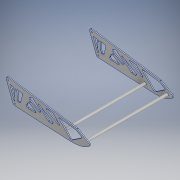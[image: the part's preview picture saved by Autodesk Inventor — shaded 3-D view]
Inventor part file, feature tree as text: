
AUTODESK INVENTOR PART (.ipt)
format: ipt  version: 2018.2 (Build 222227000, 227)  size: 1,288,192 bytes
history: native  units: mm
features: other x5, extrude x2, sketch x2, mirror x1
ambient origin geometry x8: Origin, YZ Plane, XZ Plane, XY Plane, X Axis, Y Axis, Z Axis, Center Point
bodies: Body1 (feature_tree)
feature tree (10):
  other  "bracket1.ipt"
  other  "作業平面1"
  mirror  "ミラー1"
  extrude  "押し出し1"  Depth=10.0mm
  extrude  "押し出し2"  Depth=204.0mm
  other  "ソリッド85::bracket1.ipt"
  other  "TaggingFeature1"
  sketch  "スケッチ1"
  sketch  "スケッチ2"
  other  "ソリッド1"
